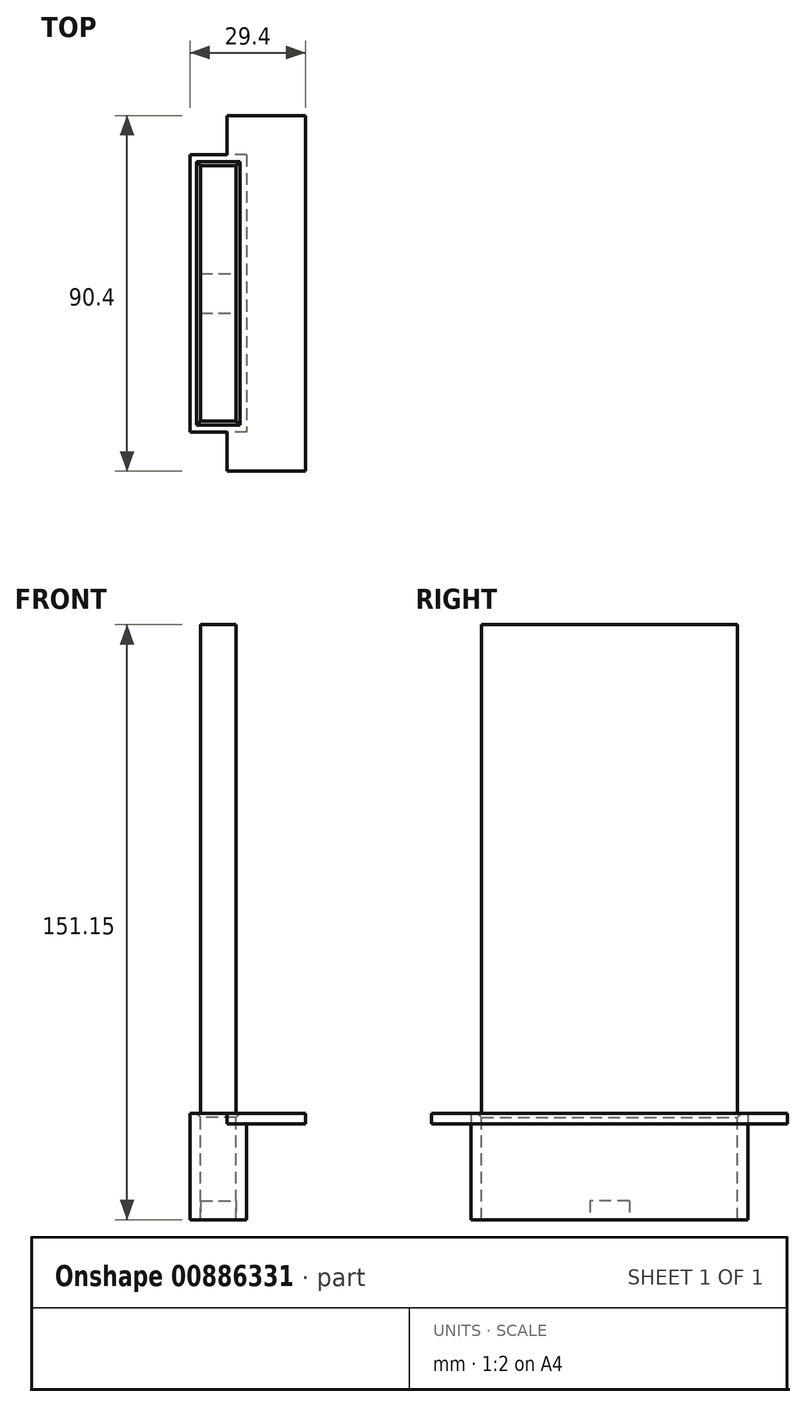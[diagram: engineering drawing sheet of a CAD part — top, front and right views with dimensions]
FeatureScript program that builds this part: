
annotation { "Feature Type Name" : "Feature", "Feature Type Description" : "" }
export const myFeature = defineFeature(function(context is Context, id is Id, definition is map)
    precondition{}
    {
        {
            var Q0;
            Q0=qCreatedBy(makeId("Top.planeOp"),FACE);
            var sketch = newSketch(context, id + "F0", { "sketchPlane" : qUnion([Q0])});
            skLineSegment(sketch, "E0.bottom", {"start": v(4.5, 32.5) * mm, "end": v(-4.5, 32.5) * mm});
            skLineSegment(sketch, "E0.top", {"start": v(4.5, -32.5) * mm, "end": v(-4.5, -32.5) * mm});
            skLineSegment(sketch, "E0.left", {"start": v(4.5, 32.5) * mm, "end": v(4.5, -32.5) * mm});
            skLineSegment(sketch, "E0.right", {"start": v(-4.5, 32.5) * mm, "end": v(-4.5, -32.5) * mm});
            skPoint(sketch, "E0.middle", {"position": v(0, 0) * mm});
            skSolve(sketch);
        }
        {
            var Q0;
            Q0=makeQuery(id+"F0.imprint","IMPRINT",FACE,{"disambiguationData":[TD([[makeQuery(id+"F0.imprint","IMPRINT",EDGE,{"derivedFrom":sQuery(id+"F0.wireOp",EDGE,"E0.bottom")}),1.0]])]});
            extrude(context, id + "F1", {"entities" : qUnion([Q0]), "depth" : 124.15 * mm, "offsetDistance" : 25 * mm});
        }
        {
            var Q0;
            Q0=qCreatedBy(makeId("Top.planeOp"),FACE);
            var sketch = newSketch(context, id + "F2", { "sketchPlane" : qUnion([Q0])});
            skLineSegment(sketch, "E1.0", {"start": v(4.5, -32.5) * mm, "end": v(-4.5, -32.5) * mm});
            skLineSegment(sketch, "E1.1", {"start": v(4.5, 32.5) * mm, "end": v(-4.5, 32.5) * mm});
            skLineSegment(sketch, "E1.2", {"start": v(4.5, 32.5) * mm, "end": v(4.5, -32.5) * mm});
            skLineSegment(sketch, "E1.3", {"start": v(-4.5, 32.5) * mm, "end": v(-4.5, -32.5) * mm});
            skLineSegment(sketch, "E2.0", {"start": v(-7.2, 35.2) * mm, "end": v(-7.2, -35.2) * mm});
            skLineSegment(sketch, "E2.1", {"start": v(7.2, 35.2) * mm, "end": v(-7.2, 35.2) * mm});
            skLineSegment(sketch, "E2.2", {"start": v(7.2, 35.2) * mm, "end": v(7.2, -35.2) * mm});
            skLineSegment(sketch, "E2.3", {"start": v(7.2, -35.2) * mm, "end": v(-7.2, -35.2) * mm});
            skSolve(sketch);
        }
        {
            var Q0;
            Q0 = qSketchRegion(id + "F2", true);
            var sketch = newSketch(context, id + "F3", { "sketchPlane" : qUnion([Q0])});
            skSolve(sketch);
        }
        {
            var Q0;
            Q0=makeQuery(id+"F3.imprint","IMPRINT",FACE,{"disambiguationData":[TD([[makeQuery(id+"F3.imprint","IMPRINT",EDGE,{"derivedFrom":makeQuery(id+"F2.imprint","IMPRINT",EDGE,{"derivedFrom":sQuery(id+"F2.wireOp",EDGE,"E1.0")})}),1.0]])]});
            extrude(context, id + "F4", {"entities" : qUnion([Q0]), "oppositeDirection" : true, "depth" : 27 * mm, "offsetDistance" : 25 * mm});
        }
        {
            var Q0;
            Q0=makeQuery(id+"F4.opExtrude","SWEPT_FACE",FACE,{"disambiguationData":[OSD([sQuery(id+"F2.wireOp",EDGE,"E2.2")])]});
            var sketch = newSketch(context, id + "F5", { "sketchPlane" : qUnion([Q0])});
            skLineSegment(sketch, "E3.bottom", {"start": v(-35.2, 0) * mm, "end": v(35.2, 0) * mm});
            skLineSegment(sketch, "E3.top", {"start": v(-35.2, -2.7) * mm, "end": v(35.2, -2.7) * mm});
            skLineSegment(sketch, "E3.left", {"start": v(-35.2, 0) * mm, "end": v(-35.2, -2.7) * mm});
            skLineSegment(sketch, "E3.right", {"start": v(35.2, 0) * mm, "end": v(35.2, -2.7) * mm});
            skSolve(sketch);
        }
        {
            var Q0;
            Q0=makeQuery(id+"F5.imprint","IMPRINT",FACE,{"disambiguationData":[TD([[makeQuery(id+"F5.imprint","IMPRINT",EDGE,{"derivedFrom":sQuery(id+"F5.wireOp",EDGE,"E3.bottom")}),1.0]])]});
            extrude(context, id + "F6", {"entities" : qUnion([Q0]), "operationType" : NewBodyOperationType.ADD, "depth" : 15 * mm, "offsetDistance" : 25 * mm});
        }
        {
            var Q0;
            Q0=makeQuery(id+"F6.boolean.opBoolean","MERGE",FACE,{"derivedFrom":[makeQuery(id+"F4.opExtrude","SWEPT_FACE",FACE,{"disambiguationData":[OSD([sQuery(id+"F2.wireOp",EDGE,"E2.3")])]}),makeQuery(id+"F6.opExtrude","SWEPT_FACE",FACE,{"disambiguationData":[OSD([sQuery(id+"F5.wireOp",EDGE,"E3.left")])]})]});
            var sketch = newSketch(context, id + "F7", { "sketchPlane" : qUnion([Q0])});
            skPoint(sketch, "E4.oppositeSnap0", {"position": v(2.2, 0) * mm});
            skLineSegment(sketch, "E4.bottom", {"start": v(22.2, 0) * mm, "end": v(2.2, 0) * mm});
            skLineSegment(sketch, "E4.top", {"start": v(22.2, -2.7) * mm, "end": v(2.2, -2.7) * mm});
            skLineSegment(sketch, "E4.left", {"start": v(22.2, 0) * mm, "end": v(22.2, -2.7) * mm});
            skLineSegment(sketch, "E4.right", {"start": v(2.2, 0) * mm, "end": v(2.2, -2.7) * mm});
            skSolve(sketch);
        }
        {
            var Q0;
            Q0=makeQuery(id+"F7.imprint","IMPRINT",FACE,{"disambiguationData":[TD([[makeQuery(id+"F7.imprint","IMPRINT",EDGE,{"derivedFrom":sQuery(id+"F7.wireOp",EDGE,"E4.bottom")}),1.0]])]});
            extrude(context, id + "F8", {"entities" : qUnion([Q0]), "depth" : 10 * mm, "offsetDistance" : 25 * mm});
        }
        {
            var Q0;
            Q0=makeQuery(id+"F8.opExtrude","SWEPT_BODY",BODY,{"disambiguationData":[OSD([sQuery(id+"F7.wireOp",EDGE,"E4.bottom"),sQuery(id+"F7.wireOp",EDGE,"E4.top"),sQuery(id+"F7.wireOp",EDGE,"E4.left"),sQuery(id+"F7.wireOp",EDGE,"E4.right")])]});
            var Q1;
            Q1=qCreatedBy(makeId("Front.planeOp"),FACE);
            mirror(context, id + "F9", {"operationType" : NewBodyOperationType.ADD, "entities" : qUnion([Q0]), "mirrorPlane" : qUnion([Q1])});
        }
        {
            var Q0;
            Q0=makeQuery(id+"F4.opExtrude","CAP_FACE",FACE,{"disambiguationData":[OSD([sQuery(id+"F2.wireOp",EDGE,"E1.0"),sQuery(id+"F2.wireOp",EDGE,"E1.1"),sQuery(id+"F2.wireOp",EDGE,"E1.2"),sQuery(id+"F2.wireOp",EDGE,"E1.3"),sQuery(id+"F2.wireOp",EDGE,"E2.0"),sQuery(id+"F2.wireOp",EDGE,"E2.1"),sQuery(id+"F2.wireOp",EDGE,"E2.2"),sQuery(id+"F2.wireOp",EDGE,"E2.3")])],"isStart":false});
            var sketch = newSketch(context, id + "F10", { "sketchPlane" : qUnion([Q0])});
            skLineSegment(sketch, "E5.bottom", {"start": v(-7.2, -5) * mm, "end": v(7.2, -5) * mm});
            skLineSegment(sketch, "E5.top", {"start": v(-7.2, 5) * mm, "end": v(7.2, 5) * mm});
            skLineSegment(sketch, "E5.left", {"start": v(-7.2, -5) * mm, "end": v(-7.2, 5) * mm});
            skLineSegment(sketch, "E5.right", {"start": v(7.2, -5) * mm, "end": v(7.2, 5) * mm});
            skPoint(sketch, "E5.middle", {"position": v(0, 0) * mm});
            skSolve(sketch);
        }
        {
            var Q0;
            {var subQ0=sQuery(id+"F10.wireOp",EDGE,"E5.bottom");var subQ1=makeQuery(id+"F4.opExtrude","CAP_EDGE",EDGE,{"disambiguationData":[OSD([sQuery(id+"F2.wireOp",EDGE,"E1.3")])],"isStart":false});var subQ2=makeQuery(id+"F10.imprint","INTERSECT",VERTEX,{"derivedFrom":[subQ1,subQ0]});Q0=makeQuery(id+"F10.imprint","IMPRINT",FACE,{"disambiguationData":[TD([[makeQuery(id+"F10.imprint","IMPRINT",EDGE,{"disambiguationData":[TD([[subQ2,-1.0]])],"derivedFrom":subQ0}),1.0]])]});}
            var Q1;
            {var subQ0=sQuery(id+"F10.wireOp",EDGE,"E5.left");Q1=makeQuery(id+"F10.imprint","IMPRINT",FACE,{"disambiguationData":[TD([[makeQuery(id+"F10.imprint","IMPRINT",EDGE,{"derivedFrom":subQ0}),-1.0]])]});}
            var Q2;
            {var subQ0=sQuery(id+"F10.wireOp",EDGE,"E5.right");Q2=makeQuery(id+"F10.imprint","IMPRINT",FACE,{"disambiguationData":[TD([[makeQuery(id+"F10.imprint","IMPRINT",EDGE,{"derivedFrom":subQ0}),1.0]])]});}
            extrude(context, id + "F11", {"entities" : qUnion([Q0, Q1, Q2]), "operationType" : NewBodyOperationType.ADD, "oppositeDirection" : true, "depth" : 4.8 * mm, "offsetDistance" : 25 * mm});
        }
        {
            var Q0;
            Q0=makeQuery(id+"F4.opExtrude","CAP_EDGE",EDGE,{"disambiguationData":[OSD([sQuery(id+"F2.wireOp",EDGE,"E1.2")])],"isStart":true});
            var Q1;
            Q1=makeQuery(id+"F4.opExtrude","CAP_EDGE",EDGE,{"disambiguationData":[OSD([sQuery(id+"F2.wireOp",EDGE,"E1.0")])],"isStart":true});
            var Q2;
            Q2=makeQuery(id+"F4.opExtrude","CAP_EDGE",EDGE,{"disambiguationData":[OSD([sQuery(id+"F2.wireOp",EDGE,"E1.3")])],"isStart":true});
            var Q3;
            Q3=makeQuery(id+"F4.opExtrude","CAP_EDGE",EDGE,{"disambiguationData":[OSD([sQuery(id+"F2.wireOp",EDGE,"E1.1")])],"isStart":true});
            chamfer(context, id + "F12", {"entities" : qUnion([Q0, Q1, Q2, Q3]), "width" : 1 * mm, "tangentPropagation" : true});
        }
    });
